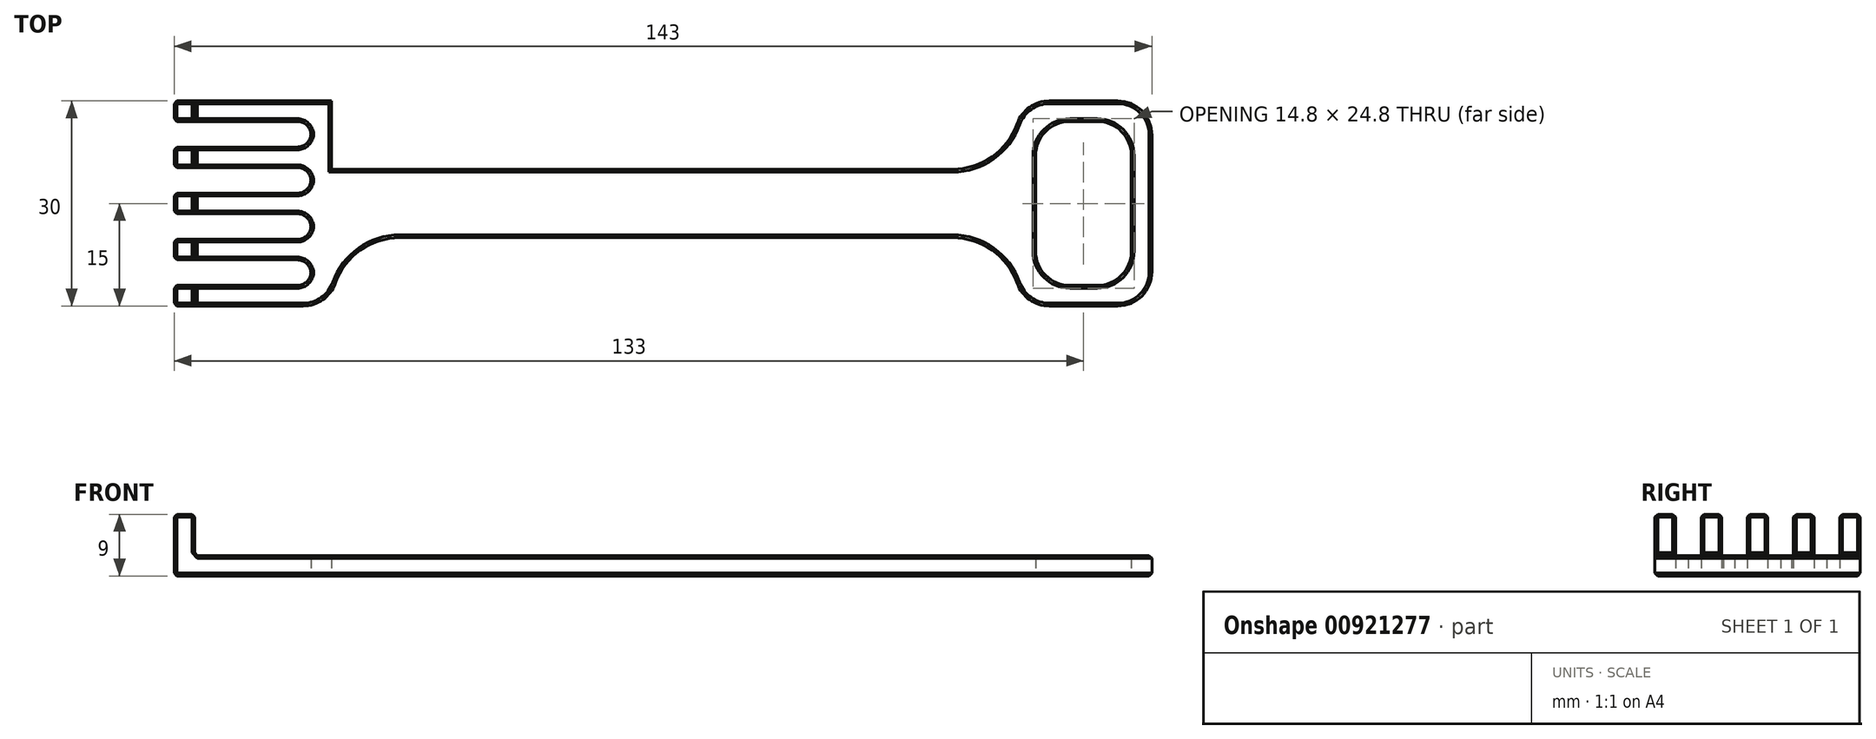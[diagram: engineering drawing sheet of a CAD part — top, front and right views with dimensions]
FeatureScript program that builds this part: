
annotation { "Feature Type Name" : "Feature", "Feature Type Description" : "" }
export const myFeature = defineFeature(function(context is Context, id is Id, definition is map)
    precondition{}
    {
        {
            var Q0;
            Q0=qCreatedBy(makeId("Top.planeOp"),FACE);
            var sketch = newSketch(context, id + "F0", { "sketchPlane" : qUnion([Q0])});
            skLineSegment(sketch, "E0.bottom", {"start": v(0, 0) * mm, "end": v(40, 0) * mm, "construction": true});
            skLineSegment(sketch, "E0.top", {"start": v(0, -30) * mm, "end": v(40, -30) * mm, "construction": true});
            skLineSegment(sketch, "E0.left", {"start": v(0, 0) * mm, "end": v(0, -30) * mm, "construction": true});
            skLineSegment(sketch, "E0.right", {"start": v(40, 0) * mm, "end": v(40, -30) * mm});
            skPoint(sketch, "E1", {"position": v(40, -15) * mm});
            skLineSegment(sketch, "E2", {"start": v(40, -15) * mm, "end": v(140, -15) * mm, "construction": true});
            skPoint(sketch, "E3", {"position": v(90, -15) * mm});
            skLineSegment(sketch, "E4.bottom", {"start": v(40, -10) * mm, "end": v(140, -10) * mm});
            skLineSegment(sketch, "E4.top", {"start": v(40, -20) * mm, "end": v(140, -20) * mm});
            skLineSegment(sketch, "E4.left", {"start": v(40, -10) * mm, "end": v(40, -20) * mm});
            skLineSegment(sketch, "E4.right", {"start": v(140, -10) * mm, "end": v(140, -20) * mm});
            skLineSegment(sketch, "E5.bottom", {"start": v(140, 0) * mm, "end": v(160, 0) * mm});
            skLineSegment(sketch, "E5.top", {"start": v(140, -30) * mm, "end": v(160, -30) * mm});
            skLineSegment(sketch, "E5.left", {"start": v(140, 0) * mm, "end": v(140, -30) * mm});
            skLineSegment(sketch, "E5.right", {"start": v(160, 0) * mm, "end": v(160, -30) * mm});
            skLineSegment(sketch, "E6.bottom", {"start": v(157, -27) * mm, "end": v(143, -27) * mm});
            skLineSegment(sketch, "E6.top", {"start": v(157, -3) * mm, "end": v(143, -3) * mm});
            skLineSegment(sketch, "E6.left", {"start": v(157, -27) * mm, "end": v(157, -3) * mm});
            skLineSegment(sketch, "E6.right", {"start": v(143, -27) * mm, "end": v(143, -3) * mm});
            skPoint(sketch, "E6.middle", {"position": v(150, -15) * mm});
            skPoint(sketch, "E6.middle.positionSnap0", {"position": v(150, 0) * mm});
            skPoint(sketch, "E6.centerSnap0", {"position": v(150, 0) * mm});
            skLineSegment(sketch, "E7.bottom", {"start": v(40, 0) * mm, "end": v(37, 0) * mm});
            skLineSegment(sketch, "E7.top", {"start": v(40, -30) * mm, "end": v(37, -30) * mm});
            skLineSegment(sketch, "E7.right", {"start": v(37, 0) * mm, "end": v(37, -30) * mm});
            skLineSegment(sketch, "E8.bottom", {"start": v(37, 0) * mm, "end": v(17, 0) * mm});
            skLineSegment(sketch, "E8.top", {"start": v(37, -3) * mm, "end": v(17, -3) * mm});
            skLineSegment(sketch, "E8.left", {"start": v(37, 0) * mm, "end": v(37, -3) * mm});
            skLineSegment(sketch, "E8.right", {"start": v(17, 0) * mm, "end": v(17, -3) * mm});
            skLineSegment(sketch, "E9.0.1.0", {"start": v(37, -6.75) * mm, "end": v(17, -6.75) * mm});
            skLineSegment(sketch, "E9.0.1.1", {"start": v(37, -9.75) * mm, "end": v(17, -9.75) * mm});
            skLineSegment(sketch, "E9.0.1.2", {"start": v(17, -6.75) * mm, "end": v(17, -9.75) * mm});
            skLineSegment(sketch, "E9.0.2.0", {"start": v(37, -13.5) * mm, "end": v(17, -13.5) * mm});
            skLineSegment(sketch, "E9.0.2.1", {"start": v(37, -16.5) * mm, "end": v(17, -16.5) * mm});
            skLineSegment(sketch, "E9.0.2.2", {"start": v(17, -13.5) * mm, "end": v(17, -16.5) * mm});
            skLineSegment(sketch, "E9.0.3.0", {"start": v(37, -20.25) * mm, "end": v(17, -20.25) * mm});
            skLineSegment(sketch, "E9.0.3.1", {"start": v(37, -23.25) * mm, "end": v(17, -23.25) * mm});
            skLineSegment(sketch, "E9.0.3.2", {"start": v(17, -20.25) * mm, "end": v(17, -23.25) * mm});
            skLineSegment(sketch, "E9.0.4.0", {"start": v(37, -27) * mm, "end": v(17, -27) * mm});
            skLineSegment(sketch, "E9.0.4.1", {"start": v(37, -30) * mm, "end": v(17, -30) * mm});
            skLineSegment(sketch, "E9.0.4.2", {"start": v(17, -27) * mm, "end": v(17, -30) * mm});
            skLineSegment(sketch, "E9.direction1", {"start": v(17, -3) * mm, "end": v(32.9, -3) * mm, "construction": true});
            skLineSegment(sketch, "E9.direction2", {"start": v(17, -3) * mm, "end": v(17, -9.75) * mm, "construction": true});
            skSolve(sketch);
        }
        {
            var Q0;
            Q0=makeQuery(id+"F0.imprint","IMPRINT",FACE,{"disambiguationData":[TD([[makeQuery(id+"F0.imprint","IMPRINT",EDGE,{"derivedFrom":sQuery(id+"F0.wireOp",EDGE,"E4.bottom")}),-1.0]])]});
            var Q1;
            {var subQ3=sQuery(id+"F0.wireOp",EDGE,"E5.bottom");Q1=makeQuery(id+"F0.imprint","IMPRINT",FACE,{"disambiguationData":[TD([[makeQuery(id+"F0.imprint","IMPRINT",EDGE,{"derivedFrom":subQ3}),-1.0]])]});}
            extrude(context, id + "F1", {"entities" : qUnion([Q0, Q1]), "depth" : 3 * mm, "offsetDistance" : 25 * mm});
        }
        {
            var Q0;
            Q0=makeQuery(id+"F0.imprint","IMPRINT",FACE,{"disambiguationData":[TD([[makeQuery(id+"F0.imprint","IMPRINT",EDGE,{"derivedFrom":sQuery(id+"F0.wireOp",EDGE,"E8.bottom")}),1.0]])]});
            var Q1;
            {var subQ10=sQuery(id+"F0.wireOp",EDGE,"E7.bottom");Q1=makeQuery(id+"F0.imprint","IMPRINT",FACE,{"disambiguationData":[TD([[makeQuery(id+"F0.imprint","IMPRINT",EDGE,{"derivedFrom":subQ10}),1.0]])]});}
            var Q2;
            {var subQ0=sQuery(id+"F0.wireOp",EDGE,"E9.0.1.0");Q2=makeQuery(id+"F0.imprint","IMPRINT",FACE,{"disambiguationData":[TD([[makeQuery(id+"F0.imprint","IMPRINT",EDGE,{"derivedFrom":subQ0}),1.0]])]});}
            var Q3;
            {var subQ0=sQuery(id+"F0.wireOp",EDGE,"E9.0.2.0");Q3=makeQuery(id+"F0.imprint","IMPRINT",FACE,{"disambiguationData":[TD([[makeQuery(id+"F0.imprint","IMPRINT",EDGE,{"derivedFrom":subQ0}),1.0]])]});}
            var Q4;
            {var subQ0=sQuery(id+"F0.wireOp",EDGE,"E9.0.3.0");Q4=makeQuery(id+"F0.imprint","IMPRINT",FACE,{"disambiguationData":[TD([[makeQuery(id+"F0.imprint","IMPRINT",EDGE,{"derivedFrom":subQ0}),1.0]])]});}
            var Q5;
            {var subQ2=sQuery(id+"F0.wireOp",EDGE,"E9.0.4.0");Q5=makeQuery(id+"F0.imprint","IMPRINT",FACE,{"disambiguationData":[TD([[makeQuery(id+"F0.imprint","IMPRINT",EDGE,{"derivedFrom":subQ2}),1.0]])]});}
            extrude(context, id + "F2", {"entities" : qUnion([Q0, Q1, Q2, Q3, Q4, Q5]), "operationType" : NewBodyOperationType.ADD, "depth" : 3 * mm, "offsetDistance" : 25 * mm});
        }
        {
            var Q0;
            {var subQ0=sQuery(id+"F0.wireOp",EDGE,"E0.right");Q0=makeQuery(id+"F2.boolean.opBoolean","MERGE",FACE,{"derivedFrom":[makeQuery(id+"F1.opExtrude","CAP_FACE",FACE,{"disambiguationData":[OSD([sQuery(id+"F0.wireOp",EDGE,"E4.bottom"),sQuery(id+"F0.wireOp",EDGE,"E4.top"),sQuery(id+"F0.wireOp",EDGE,"E5.bottom"),sQuery(id+"F0.wireOp",EDGE,"E5.top"),sQuery(id+"F0.wireOp",EDGE,"E5.left"),sQuery(id+"F0.wireOp",EDGE,"E5.right"),sQuery(id+"F0.wireOp",EDGE,"E6.bottom"),sQuery(id+"F0.wireOp",EDGE,"E6.top"),sQuery(id+"F0.wireOp",EDGE,"E6.left"),sQuery(id+"F0.wireOp",EDGE,"E6.right"),subQ0])],"isStart":false}),makeQuery(id+"F2.opExtrude","CAP_FACE",FACE,{"disambiguationData":[OSD([sQuery(id+"F0.wireOp",EDGE,"E7.bottom"),sQuery(id+"F0.wireOp",EDGE,"E7.top"),subQ0,sQuery(id+"F0.wireOp",EDGE,"E7.right"),sQuery(id+"F0.wireOp",EDGE,"E8.bottom"),sQuery(id+"F0.wireOp",EDGE,"E8.top"),sQuery(id+"F0.wireOp",EDGE,"E8.right"),sQuery(id+"F0.wireOp",EDGE,"E9.0.1.0"),sQuery(id+"F0.wireOp",EDGE,"E9.0.1.1"),sQuery(id+"F0.wireOp",EDGE,"E9.0.1.2"),sQuery(id+"F0.wireOp",EDGE,"E9.0.2.0"),sQuery(id+"F0.wireOp",EDGE,"E9.0.2.1"),sQuery(id+"F0.wireOp",EDGE,"E9.0.2.2"),sQuery(id+"F0.wireOp",EDGE,"E9.0.3.0"),sQuery(id+"F0.wireOp",EDGE,"E9.0.3.1"),sQuery(id+"F0.wireOp",EDGE,"E9.0.3.2"),sQuery(id+"F0.wireOp",EDGE,"E9.0.4.0"),sQuery(id+"F0.wireOp",EDGE,"E9.0.4.1"),sQuery(id+"F0.wireOp",EDGE,"E9.0.4.2")])],"isStart":false})]});}
            var sketch = newSketch(context, id + "F3", { "sketchPlane" : qUnion([Q0])});
            skLineSegment(sketch, "E10.bottom", {"start": v(17, 0) * mm, "end": v(20, 0) * mm});
            skLineSegment(sketch, "E10.top", {"start": v(17, -3) * mm, "end": v(20, -3) * mm});
            skLineSegment(sketch, "E10.left", {"start": v(17, 0) * mm, "end": v(17, -3) * mm});
            skLineSegment(sketch, "E10.right", {"start": v(20, 0) * mm, "end": v(20, -3) * mm});
            skLineSegment(sketch, "E11.bottom", {"start": v(17, -6.75) * mm, "end": v(20, -6.75) * mm});
            skLineSegment(sketch, "E11.top", {"start": v(17, -9.75) * mm, "end": v(20, -9.75) * mm});
            skLineSegment(sketch, "E11.left", {"start": v(17, -6.75) * mm, "end": v(17, -9.75) * mm});
            skLineSegment(sketch, "E11.right", {"start": v(20, -6.75) * mm, "end": v(20, -9.75) * mm});
            skLineSegment(sketch, "E12.bottom", {"start": v(17, -13.5) * mm, "end": v(20, -13.5) * mm});
            skLineSegment(sketch, "E12.top", {"start": v(17, -16.5) * mm, "end": v(20, -16.5) * mm});
            skLineSegment(sketch, "E12.left", {"start": v(17, -13.5) * mm, "end": v(17, -16.5) * mm});
            skLineSegment(sketch, "E12.right", {"start": v(20, -13.5) * mm, "end": v(20, -16.5) * mm});
            skLineSegment(sketch, "E13.bottom", {"start": v(17, -20.25) * mm, "end": v(20, -20.25) * mm});
            skLineSegment(sketch, "E13.top", {"start": v(17, -23.25) * mm, "end": v(20, -23.25) * mm});
            skLineSegment(sketch, "E13.left", {"start": v(17, -20.25) * mm, "end": v(17, -23.25) * mm});
            skLineSegment(sketch, "E13.right", {"start": v(20, -20.25) * mm, "end": v(20, -23.25) * mm});
            skLineSegment(sketch, "E14.bottom", {"start": v(17, -27) * mm, "end": v(20, -27) * mm});
            skLineSegment(sketch, "E14.top", {"start": v(17, -30) * mm, "end": v(20, -30) * mm});
            skLineSegment(sketch, "E14.left", {"start": v(17, -27) * mm, "end": v(17, -30) * mm});
            skLineSegment(sketch, "E14.right", {"start": v(20, -27) * mm, "end": v(20, -30) * mm});
            skSolve(sketch);
        }
        {
            var Q0;
            Q0=makeQuery(id+"F3.imprint","IMPRINT",FACE,{"disambiguationData":[TD([[makeQuery(id+"F3.imprint","IMPRINT",EDGE,{"derivedFrom":sQuery(id+"F3.wireOp",EDGE,"E10.bottom")}),1.0]])]});
            var Q1;
            Q1=makeQuery(id+"F3.imprint","IMPRINT",FACE,{"disambiguationData":[TD([[makeQuery(id+"F3.imprint","IMPRINT",EDGE,{"derivedFrom":sQuery(id+"F3.wireOp",EDGE,"E11.bottom")}),1.0]])]});
            var Q2;
            Q2=makeQuery(id+"F3.imprint","IMPRINT",FACE,{"disambiguationData":[TD([[makeQuery(id+"F3.imprint","IMPRINT",EDGE,{"derivedFrom":sQuery(id+"F3.wireOp",EDGE,"E12.bottom")}),1.0]])]});
            var Q3;
            Q3=makeQuery(id+"F3.imprint","IMPRINT",FACE,{"disambiguationData":[TD([[makeQuery(id+"F3.imprint","IMPRINT",EDGE,{"derivedFrom":sQuery(id+"F3.wireOp",EDGE,"E13.bottom")}),1.0]])]});
            var Q4;
            Q4=makeQuery(id+"F3.imprint","IMPRINT",FACE,{"disambiguationData":[TD([[makeQuery(id+"F3.imprint","IMPRINT",EDGE,{"derivedFrom":sQuery(id+"F3.wireOp",EDGE,"E14.bottom")}),1.0]])]});
            extrude(context, id + "F4", {"entities" : qUnion([Q0, Q1, Q2, Q3, Q4]), "operationType" : NewBodyOperationType.ADD, "depth" : 6 * mm, "offsetDistance" : 25 * mm});
        }
        {
            var Q0;
            Q0=makeQuery(id+"F1.opExtrude","SWEPT_EDGE",EDGE,{"disambiguationData":[OSD([sQuery(id+"F0.wireOp",EDGE,"E6.top"),sQuery(id+"F0.wireOp",EDGE,"E6.right")])]});
            var Q1;
            Q1=makeQuery(id+"F1.opExtrude","SWEPT_EDGE",EDGE,{"disambiguationData":[OSD([sQuery(id+"F0.wireOp",EDGE,"E6.top"),sQuery(id+"F0.wireOp",EDGE,"E6.left")])]});
            var Q2;
            Q2=makeQuery(id+"F1.opExtrude","SWEPT_EDGE",EDGE,{"disambiguationData":[OSD([sQuery(id+"F0.wireOp",EDGE,"E6.bottom"),sQuery(id+"F0.wireOp",EDGE,"E6.left")])]});
            var Q3;
            Q3=makeQuery(id+"F1.opExtrude","SWEPT_EDGE",EDGE,{"disambiguationData":[OSD([sQuery(id+"F0.wireOp",EDGE,"E6.bottom"),sQuery(id+"F0.wireOp",EDGE,"E6.right")])]});
            var Q4;
            Q4=makeQuery(id+"F1.opExtrude","SWEPT_EDGE",EDGE,{"disambiguationData":[OSD([sQuery(id+"F0.wireOp",EDGE,"E5.bottom"),sQuery(id+"F0.wireOp",EDGE,"E5.left")])]});
            var Q5;
            Q5=makeQuery(id+"F1.opExtrude","SWEPT_EDGE",EDGE,{"disambiguationData":[OSD([sQuery(id+"F0.wireOp",EDGE,"E5.top"),sQuery(id+"F0.wireOp",EDGE,"E5.right")])]});
            var Q6;
            Q6=makeQuery(id+"F1.opExtrude","SWEPT_EDGE",EDGE,{"disambiguationData":[OSD([sQuery(id+"F0.wireOp",EDGE,"E5.bottom"),sQuery(id+"F0.wireOp",EDGE,"E5.right")])]});
            var Q7;
            Q7=makeQuery(id+"F1.opExtrude","SWEPT_EDGE",EDGE,{"disambiguationData":[OSD([sQuery(id+"F0.wireOp",EDGE,"E5.top"),sQuery(id+"F0.wireOp",EDGE,"E5.left")])]});
            fillet(context, id + "F5", {"entities" : qUnion([Q0, Q1, Q2, Q3, Q4, Q5, Q6, Q7]), "radius" : 5 * mm, "tangentPropagation" : true, "allowEdgeOverflow" : false});
        }
        {
            var Q0;
            Q0=makeQuery(id+"F1.opExtrude","SWEPT_EDGE",EDGE,{"disambiguationData":[OSD([sQuery(id+"F0.wireOp",EDGE,"E4.top"),sQuery(id+"F0.wireOp",EDGE,"E5.left")])]});
            var Q1;
            Q1=makeQuery(id+"F1.opExtrude","SWEPT_EDGE",EDGE,{"disambiguationData":[OSD([sQuery(id+"F0.wireOp",EDGE,"E4.bottom"),sQuery(id+"F0.wireOp",EDGE,"E5.left")])]});
            fillet(context, id + "F6", {"entities" : qUnion([Q0, Q1]), "radius" : 10 * mm, "tangentPropagation" : true, "allowEdgeOverflow" : false});
        }
        {
            var Q0;
            Q0=makeQuery(id+"F1.opExtrude","SWEPT_EDGE",EDGE,{"disambiguationData":[OSD([sQuery(id+"F0.wireOp",EDGE,"E4.bottom"),sQuery(id+"F0.wireOp",EDGE,"E0.right")])]});
            var Q1;
            Q1=makeQuery(id+"F1.opExtrude","SWEPT_EDGE",EDGE,{"disambiguationData":[OSD([sQuery(id+"F0.wireOp",EDGE,"E4.top"),sQuery(id+"F0.wireOp",EDGE,"E0.right")])]});
            fillet(context, id + "F7", {"entities" : qUnion([Q0, Q1]), "radius" : 10 * mm, "tangentPropagation" : true, "allowEdgeOverflow" : false});
        }
        {
            var Q0;
            Q0=makeQuery(id+"F2.opExtrude","SWEPT_EDGE",EDGE,{"disambiguationData":[OSD([sQuery(id+"F0.wireOp",EDGE,"E7.right"),sQuery(id+"F0.wireOp",EDGE,"E8.top"),sQuery(id+"F0.wireOp",EDGE,"E8.left")])]});
            var Q1;
            Q1=makeQuery(id+"F2.opExtrude","SWEPT_EDGE",EDGE,{"disambiguationData":[OSD([sQuery(id+"F0.wireOp",EDGE,"E7.right"),sQuery(id+"F0.wireOp",EDGE,"E9.0.1.0")])]});
            var Q2;
            Q2=makeQuery(id+"F2.opExtrude","SWEPT_EDGE",EDGE,{"disambiguationData":[OSD([sQuery(id+"F0.wireOp",EDGE,"E7.right"),sQuery(id+"F0.wireOp",EDGE,"E9.0.1.1")])]});
            var Q3;
            Q3=makeQuery(id+"F2.opExtrude","SWEPT_EDGE",EDGE,{"disambiguationData":[OSD([sQuery(id+"F0.wireOp",EDGE,"E7.right"),sQuery(id+"F0.wireOp",EDGE,"E9.0.2.0")])]});
            var Q4;
            Q4=makeQuery(id+"F2.opExtrude","SWEPT_EDGE",EDGE,{"disambiguationData":[OSD([sQuery(id+"F0.wireOp",EDGE,"E7.right"),sQuery(id+"F0.wireOp",EDGE,"E9.0.2.1")])]});
            var Q5;
            Q5=makeQuery(id+"F2.opExtrude","SWEPT_EDGE",EDGE,{"disambiguationData":[OSD([sQuery(id+"F0.wireOp",EDGE,"E7.right"),sQuery(id+"F0.wireOp",EDGE,"E9.0.3.0")])]});
            var Q6;
            Q6=makeQuery(id+"F2.opExtrude","SWEPT_EDGE",EDGE,{"disambiguationData":[OSD([sQuery(id+"F0.wireOp",EDGE,"E7.right"),sQuery(id+"F0.wireOp",EDGE,"E9.0.3.1")])]});
            var Q7;
            Q7=makeQuery(id+"F2.opExtrude","SWEPT_EDGE",EDGE,{"disambiguationData":[OSD([sQuery(id+"F0.wireOp",EDGE,"E7.right"),sQuery(id+"F0.wireOp",EDGE,"E9.0.4.0")])]});
            fillet(context, id + "F8", {"entities" : qUnion([Q0, Q1, Q2, Q3, Q4, Q5, Q6, Q7]), "radius" : 2 * mm, "tangentPropagation" : true, "allowEdgeOverflow" : false});
        }
        {
            var Q0;
            Q0=makeQuery(id+"F7.opFillet","BLEND_EDGE",EDGE,{"blendedFrom":[makeQuery(id+"F1.opExtrude","SWEPT_EDGE",EDGE,{"disambiguationData":[OSD([sQuery(id+"F0.wireOp",EDGE,"E4.bottom"),sQuery(id+"F0.wireOp",EDGE,"E0.right")])]}),makeQuery(id+"F4.boolean.opBoolean","MERGE",FACE,{"derivedFrom":[makeQuery(id+"F2.opExtrude","SWEPT_FACE",FACE,{"disambiguationData":[OSD([sQuery(id+"F0.wireOp",EDGE,"E7.bottom"),sQuery(id+"F0.wireOp",EDGE,"E8.bottom")])]}),makeQuery(id+"F4.opExtrude","SWEPT_FACE",FACE,{"disambiguationData":[OSD([sQuery(id+"F3.wireOp",EDGE,"E10.bottom")])]})]})],"blendedInto":[makeQuery(id+"F4.boolean.opBoolean","MERGE",FACE,{"derivedFrom":[makeQuery(id+"F2.opExtrude","SWEPT_FACE",FACE,{"disambiguationData":[OSD([sQuery(id+"F0.wireOp",EDGE,"E7.bottom"),sQuery(id+"F0.wireOp",EDGE,"E8.bottom")])]}),makeQuery(id+"F4.opExtrude","SWEPT_FACE",FACE,{"disambiguationData":[OSD([sQuery(id+"F3.wireOp",EDGE,"E10.bottom")])]})]})]});
            var Q1;
            Q1=makeQuery(id+"F7.opFillet","BLEND_EDGE",EDGE,{"blendedFrom":[makeQuery(id+"F1.opExtrude","SWEPT_EDGE",EDGE,{"disambiguationData":[OSD([sQuery(id+"F0.wireOp",EDGE,"E4.top"),sQuery(id+"F0.wireOp",EDGE,"E0.right")])]}),makeQuery(id+"F4.boolean.opBoolean","MERGE",FACE,{"derivedFrom":[makeQuery(id+"F2.opExtrude","SWEPT_FACE",FACE,{"disambiguationData":[OSD([sQuery(id+"F0.wireOp",EDGE,"E7.top"),sQuery(id+"F0.wireOp",EDGE,"E9.0.4.1")])]}),makeQuery(id+"F4.opExtrude","SWEPT_FACE",FACE,{"disambiguationData":[OSD([sQuery(id+"F3.wireOp",EDGE,"E14.top")])]})]})],"blendedInto":[makeQuery(id+"F4.boolean.opBoolean","MERGE",FACE,{"derivedFrom":[makeQuery(id+"F2.opExtrude","SWEPT_FACE",FACE,{"disambiguationData":[OSD([sQuery(id+"F0.wireOp",EDGE,"E7.top"),sQuery(id+"F0.wireOp",EDGE,"E9.0.4.1")])]}),makeQuery(id+"F4.opExtrude","SWEPT_FACE",FACE,{"disambiguationData":[OSD([sQuery(id+"F3.wireOp",EDGE,"E14.top")])]})]})]});
            fillet(context, id + "F9", {"entities" : qUnion([Q0, Q1]), "radius" : 5 * mm, "tangentPropagation" : true, "allowEdgeOverflow" : false});
        }
        {
            var Q0;
            {var subQ0=sQuery(id+"F0.wireOp",EDGE,"E0.right");Q0=makeQuery(id+"F2.boolean.opBoolean","MERGE",FACE,{"derivedFrom":[makeQuery(id+"F1.opExtrude","CAP_FACE",FACE,{"disambiguationData":[OSD([sQuery(id+"F0.wireOp",EDGE,"E4.bottom"),sQuery(id+"F0.wireOp",EDGE,"E4.top"),sQuery(id+"F0.wireOp",EDGE,"E5.bottom"),sQuery(id+"F0.wireOp",EDGE,"E5.top"),sQuery(id+"F0.wireOp",EDGE,"E5.left"),sQuery(id+"F0.wireOp",EDGE,"E5.right"),sQuery(id+"F0.wireOp",EDGE,"E6.bottom"),sQuery(id+"F0.wireOp",EDGE,"E6.top"),sQuery(id+"F0.wireOp",EDGE,"E6.left"),sQuery(id+"F0.wireOp",EDGE,"E6.right"),subQ0])],"isStart":true}),makeQuery(id+"F2.opExtrude","CAP_FACE",FACE,{"disambiguationData":[OSD([sQuery(id+"F0.wireOp",EDGE,"E7.bottom"),sQuery(id+"F0.wireOp",EDGE,"E7.top"),subQ0,sQuery(id+"F0.wireOp",EDGE,"E7.right"),sQuery(id+"F0.wireOp",EDGE,"E8.bottom"),sQuery(id+"F0.wireOp",EDGE,"E8.top"),sQuery(id+"F0.wireOp",EDGE,"E8.right"),sQuery(id+"F0.wireOp",EDGE,"E9.0.1.0"),sQuery(id+"F0.wireOp",EDGE,"E9.0.1.1"),sQuery(id+"F0.wireOp",EDGE,"E9.0.1.2"),sQuery(id+"F0.wireOp",EDGE,"E9.0.2.0"),sQuery(id+"F0.wireOp",EDGE,"E9.0.2.1"),sQuery(id+"F0.wireOp",EDGE,"E9.0.2.2"),sQuery(id+"F0.wireOp",EDGE,"E9.0.3.0"),sQuery(id+"F0.wireOp",EDGE,"E9.0.3.1"),sQuery(id+"F0.wireOp",EDGE,"E9.0.3.2"),sQuery(id+"F0.wireOp",EDGE,"E9.0.4.0"),sQuery(id+"F0.wireOp",EDGE,"E9.0.4.1"),sQuery(id+"F0.wireOp",EDGE,"E9.0.4.2")])],"isStart":true})]});}
            var Q1;
            {var subQ0=sQuery(id+"F0.wireOp",EDGE,"E0.right");Q1=makeQuery(id+"F2.boolean.opBoolean","MERGE",FACE,{"derivedFrom":[makeQuery(id+"F1.opExtrude","CAP_FACE",FACE,{"disambiguationData":[OSD([sQuery(id+"F0.wireOp",EDGE,"E4.bottom"),sQuery(id+"F0.wireOp",EDGE,"E4.top"),sQuery(id+"F0.wireOp",EDGE,"E5.bottom"),sQuery(id+"F0.wireOp",EDGE,"E5.top"),sQuery(id+"F0.wireOp",EDGE,"E5.left"),sQuery(id+"F0.wireOp",EDGE,"E5.right"),sQuery(id+"F0.wireOp",EDGE,"E6.bottom"),sQuery(id+"F0.wireOp",EDGE,"E6.top"),sQuery(id+"F0.wireOp",EDGE,"E6.left"),sQuery(id+"F0.wireOp",EDGE,"E6.right"),subQ0])],"isStart":false}),makeQuery(id+"F2.opExtrude","CAP_FACE",FACE,{"disambiguationData":[OSD([sQuery(id+"F0.wireOp",EDGE,"E7.bottom"),sQuery(id+"F0.wireOp",EDGE,"E7.top"),subQ0,sQuery(id+"F0.wireOp",EDGE,"E7.right"),sQuery(id+"F0.wireOp",EDGE,"E8.bottom"),sQuery(id+"F0.wireOp",EDGE,"E8.top"),sQuery(id+"F0.wireOp",EDGE,"E8.right"),sQuery(id+"F0.wireOp",EDGE,"E9.0.1.0"),sQuery(id+"F0.wireOp",EDGE,"E9.0.1.1"),sQuery(id+"F0.wireOp",EDGE,"E9.0.1.2"),sQuery(id+"F0.wireOp",EDGE,"E9.0.2.0"),sQuery(id+"F0.wireOp",EDGE,"E9.0.2.1"),sQuery(id+"F0.wireOp",EDGE,"E9.0.2.2"),sQuery(id+"F0.wireOp",EDGE,"E9.0.3.0"),sQuery(id+"F0.wireOp",EDGE,"E9.0.3.1"),sQuery(id+"F0.wireOp",EDGE,"E9.0.3.2"),sQuery(id+"F0.wireOp",EDGE,"E9.0.4.0"),sQuery(id+"F0.wireOp",EDGE,"E9.0.4.1"),sQuery(id+"F0.wireOp",EDGE,"E9.0.4.2")])],"isStart":false})]});}
            var Q2;
            Q2=makeQuery(id+"F4.boolean.opBoolean","MERGE",FACE,{"derivedFrom":[makeQuery(id+"F2.opExtrude","SWEPT_FACE",FACE,{"disambiguationData":[OSD([sQuery(id+"F0.wireOp",EDGE,"E9.0.4.2")])]}),makeQuery(id+"F4.opExtrude","SWEPT_FACE",FACE,{"disambiguationData":[OSD([sQuery(id+"F3.wireOp",EDGE,"E14.left")])]})]});
            var Q3;
            Q3=makeQuery(id+"F4.boolean.opBoolean","MERGE",FACE,{"derivedFrom":[makeQuery(id+"F2.opExtrude","SWEPT_FACE",FACE,{"disambiguationData":[OSD([sQuery(id+"F0.wireOp",EDGE,"E9.0.3.2")])]}),makeQuery(id+"F4.opExtrude","SWEPT_FACE",FACE,{"disambiguationData":[OSD([sQuery(id+"F3.wireOp",EDGE,"E13.left")])]})]});
            var Q4;
            Q4=makeQuery(id+"F4.boolean.opBoolean","MERGE",FACE,{"derivedFrom":[makeQuery(id+"F2.opExtrude","SWEPT_FACE",FACE,{"disambiguationData":[OSD([sQuery(id+"F0.wireOp",EDGE,"E9.0.2.2")])]}),makeQuery(id+"F4.opExtrude","SWEPT_FACE",FACE,{"disambiguationData":[OSD([sQuery(id+"F3.wireOp",EDGE,"E12.left")])]})]});
            var Q5;
            Q5=makeQuery(id+"F4.boolean.opBoolean","MERGE",FACE,{"derivedFrom":[makeQuery(id+"F2.opExtrude","SWEPT_FACE",FACE,{"disambiguationData":[OSD([sQuery(id+"F0.wireOp",EDGE,"E9.0.1.2")])]}),makeQuery(id+"F4.opExtrude","SWEPT_FACE",FACE,{"disambiguationData":[OSD([sQuery(id+"F3.wireOp",EDGE,"E11.left")])]})]});
            var Q6;
            Q6=makeQuery(id+"F4.boolean.opBoolean","MERGE",FACE,{"derivedFrom":[makeQuery(id+"F2.opExtrude","SWEPT_FACE",FACE,{"disambiguationData":[OSD([sQuery(id+"F0.wireOp",EDGE,"E8.right")])]}),makeQuery(id+"F4.opExtrude","SWEPT_FACE",FACE,{"disambiguationData":[OSD([sQuery(id+"F3.wireOp",EDGE,"E10.left")])]})]});
            var Q7;
            Q7=makeQuery(id+"F4.opExtrude","CAP_FACE",FACE,{"disambiguationData":[OSD([sQuery(id+"F3.wireOp",EDGE,"E10.bottom"),sQuery(id+"F3.wireOp",EDGE,"E10.top"),sQuery(id+"F3.wireOp",EDGE,"E10.left"),sQuery(id+"F3.wireOp",EDGE,"E10.right")])],"isStart":false});
            var Q8;
            Q8=makeQuery(id+"F4.opExtrude","CAP_FACE",FACE,{"disambiguationData":[OSD([sQuery(id+"F3.wireOp",EDGE,"E11.bottom"),sQuery(id+"F3.wireOp",EDGE,"E11.top"),sQuery(id+"F3.wireOp",EDGE,"E11.left"),sQuery(id+"F3.wireOp",EDGE,"E11.right")])],"isStart":false});
            var Q9;
            Q9=makeQuery(id+"F4.opExtrude","CAP_FACE",FACE,{"disambiguationData":[OSD([sQuery(id+"F3.wireOp",EDGE,"E12.bottom"),sQuery(id+"F3.wireOp",EDGE,"E12.top"),sQuery(id+"F3.wireOp",EDGE,"E12.left"),sQuery(id+"F3.wireOp",EDGE,"E12.right")])],"isStart":false});
            var Q10;
            Q10=makeQuery(id+"F4.opExtrude","CAP_FACE",FACE,{"disambiguationData":[OSD([sQuery(id+"F3.wireOp",EDGE,"E13.bottom"),sQuery(id+"F3.wireOp",EDGE,"E13.top"),sQuery(id+"F3.wireOp",EDGE,"E13.left"),sQuery(id+"F3.wireOp",EDGE,"E13.right")])],"isStart":false});
            var Q11;
            Q11=makeQuery(id+"F4.opExtrude","CAP_FACE",FACE,{"disambiguationData":[OSD([sQuery(id+"F3.wireOp",EDGE,"E14.bottom"),sQuery(id+"F3.wireOp",EDGE,"E14.top"),sQuery(id+"F3.wireOp",EDGE,"E14.left"),sQuery(id+"F3.wireOp",EDGE,"E14.right")])],"isStart":false});
            chamfer(context, id + "F10", {"entities" : qUnion([Q0, Q1, Q2, Q3, Q4, Q5, Q6, Q7, Q8, Q9, Q10, Q11]), "width" : 0.4 * mm, "tangentPropagation" : true});
        }
    });
